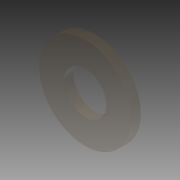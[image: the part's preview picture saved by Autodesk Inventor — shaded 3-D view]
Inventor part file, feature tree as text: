
AUTODESK INVENTOR PART (.ipt)
format: ipt  version: 2013 (Build 170138000, 138)  size: 73,728 bytes
history: native  units: mm (DEFAULTED — no unit token found)
features: extrude x1, sketch x1
ambient origin geometry x8: Origin, YZ Plane, XZ Plane, XY Plane, X Axis, Y Axis, Z Axis, Center Point
bodies: Solid1 (feature_tree)
feature tree (2):
  extrude  "Extrusion1"  Depth=4.3942mm
  sketch  "Sketch1"  dims[d0=9.525mm d1=4.3942mm d2=1.016mm d3=0.0mm]
